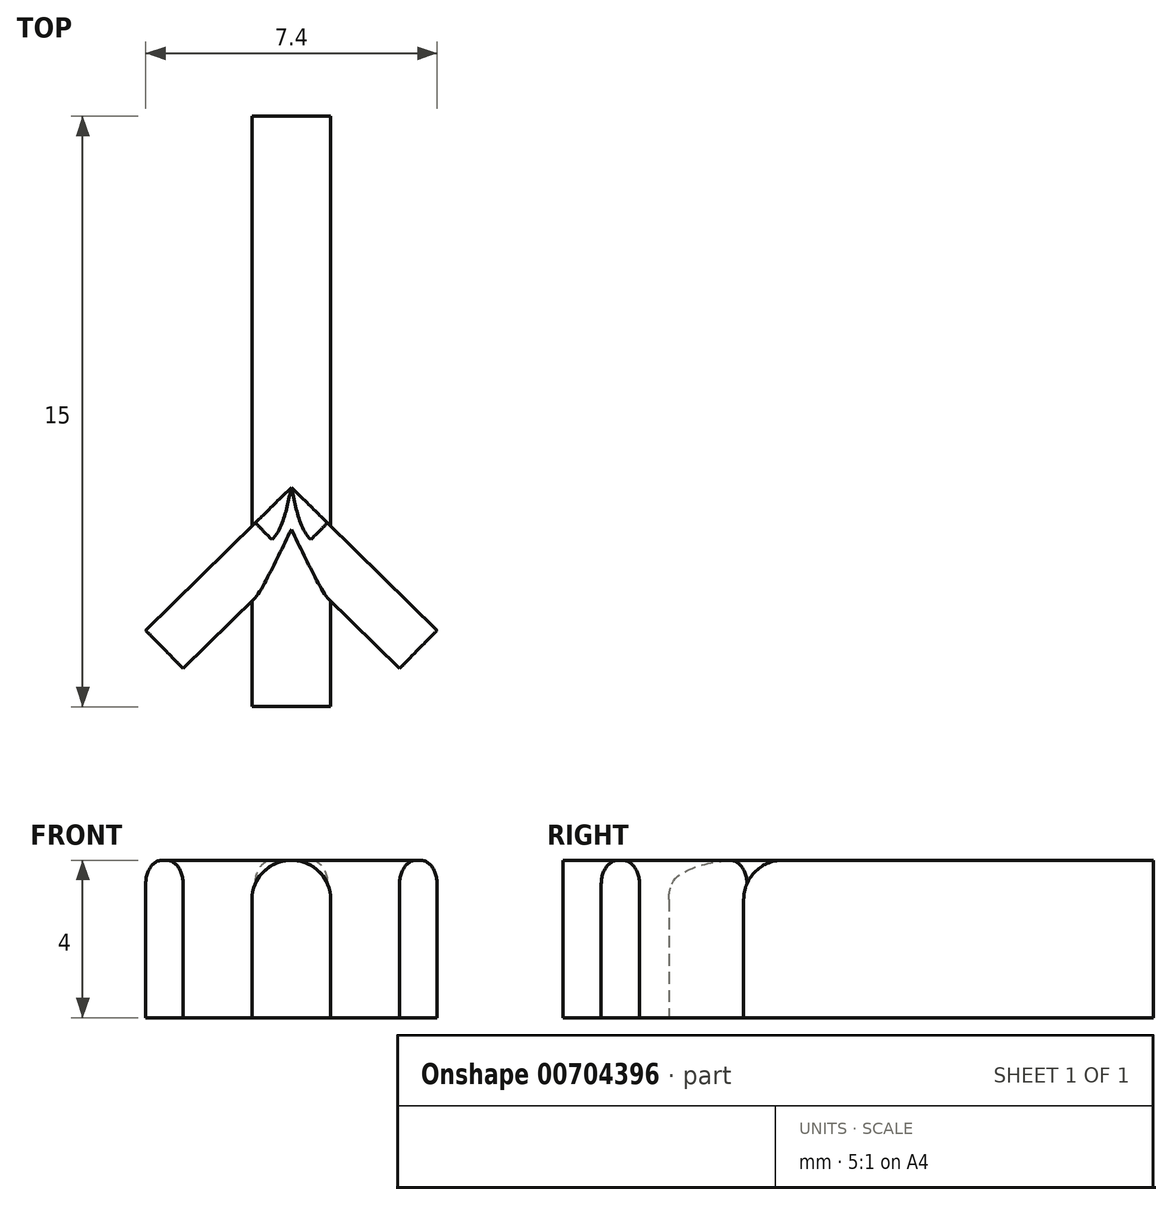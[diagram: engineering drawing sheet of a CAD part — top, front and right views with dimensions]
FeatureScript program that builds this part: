
annotation { "Feature Type Name" : "Feature", "Feature Type Description" : "" }
export const myFeature = defineFeature(function(context is Context, id is Id, definition is map)
    precondition{}
    {
        {
            var Q0;
            Q0=qCreatedBy(makeId("Top.planeOp"),FACE);
            var sketch = newSketch(context, id + "F0", { "sketchPlane" : qUnion([Q0])});
            skLineSegment(sketch, "E0", {"start": v(-1, 3.24) * mm, "end": v(-1, -7.17) * mm});
            skLineSegment(sketch, "E1", {"start": v(-1, 3.24) * mm, "end": v(0, 3.24) * mm});
            skLineSegment(sketch, "E2", {"start": v(-1, -7.17) * mm, "end": v(-3.7, -9.82) * mm});
            skLineSegment(sketch, "E3", {"start": v(-3.7, -9.82) * mm, "end": v(-2.75, -10.79) * mm});
            skLineSegment(sketch, "E4", {"start": v(-2.75, -10.79) * mm, "end": v(-1, -9.07) * mm});
            skLineSegment(sketch, "E5", {"start": v(-1, -9.07) * mm, "end": v(-1, -11.76) * mm});
            skLineSegment(sketch, "E6", {"start": v(-1, -11.76) * mm, "end": v(0, -11.76) * mm});
            skLineSegment(sketch, "E7.MirrorCS", {"start": v(1, 3.24) * mm, "end": v(0, 3.24) * mm});
            skLineSegment(sketch, "E8.MirrorCS", {"start": v(1, 3.24) * mm, "end": v(1, -7.17) * mm});
            skLineSegment(sketch, "E9.MirrorCS", {"start": v(1, -7.17) * mm, "end": v(3.7, -9.82) * mm});
            skLineSegment(sketch, "E10.MirrorCS", {"start": v(3.7, -9.82) * mm, "end": v(2.75, -10.79) * mm});
            skLineSegment(sketch, "E11.MirrorCS", {"start": v(2.75, -10.79) * mm, "end": v(1, -9.07) * mm});
            skLineSegment(sketch, "E12.MirrorCS", {"start": v(1, -9.07) * mm, "end": v(1, -11.76) * mm});
            skLineSegment(sketch, "E13.MirrorCS", {"start": v(1, -11.76) * mm, "end": v(0, -11.76) * mm});
            skSolve(sketch);
        }
        {
            var Q0;
            Q0=makeQuery(id+"F0.imprint","IMPRINT",FACE,{"disambiguationData":[TD([[makeQuery(id+"F0.imprint","IMPRINT",EDGE,{"derivedFrom":sQuery(id+"F0.wireOp",EDGE,"E0")}),1.0]])]});
            extrude(context, id + "F1", {"entities" : qUnion([Q0]), "depth" : 4 * mm, "offsetDistance" : 25 * mm});
        }
        {
            var Q0;
            Q0=makeQuery(id+"F1.opExtrude","CAP_EDGE",EDGE,{"disambiguationData":[OSD([sQuery(id+"F0.wireOp",EDGE,"E0")])],"isStart":false});
            var Q1;
            Q1=makeQuery(id+"F1.opExtrude","CAP_EDGE",EDGE,{"disambiguationData":[OSD([sQuery(id+"F0.wireOp",EDGE,"E8.MirrorCS")])],"isStart":false});
            fillet(context, id + "F2", {"entities" : qUnion([Q0, Q1]), "radius" : 1 * mm, "tangentPropagation" : true, "allowEdgeOverflow" : false});
        }
        {
            var Q0;
            Q0=makeQuery(id+"F1.opExtrude","CAP_EDGE",EDGE,{"disambiguationData":[OSD([sQuery(id+"F0.wireOp",EDGE,"E4")])],"isStart":false});
            var Q1;
            Q1=makeQuery(id+"F1.opExtrude","CAP_EDGE",EDGE,{"disambiguationData":[OSD([sQuery(id+"F0.wireOp",EDGE,"E2")])],"isStart":false});
            var Q2;
            Q2=makeQuery(id+"F1.opExtrude","CAP_EDGE",EDGE,{"disambiguationData":[OSD([sQuery(id+"F0.wireOp",EDGE,"E9.MirrorCS")])],"isStart":false});
            var Q3;
            Q3=makeQuery(id+"F1.opExtrude","CAP_EDGE",EDGE,{"disambiguationData":[OSD([sQuery(id+"F0.wireOp",EDGE,"E11.MirrorCS")])],"isStart":false});
            fillet(context, id + "F3", {"entities" : qUnion([Q0, Q1, Q2, Q3]), "radius" : 0.6 * mm, "tangentPropagation" : true, "allowEdgeOverflow" : false});
        }
        {
            var Q0;
            Q0=makeQuery(id+"F1.opExtrude","CAP_EDGE",EDGE,{"disambiguationData":[OSD([sQuery(id+"F0.wireOp",EDGE,"E5")])],"isStart":false});
            var Q1;
            Q1=makeQuery(id+"F1.opExtrude","CAP_EDGE",EDGE,{"disambiguationData":[OSD([sQuery(id+"F0.wireOp",EDGE,"E12.MirrorCS")])],"isStart":false});
            fillet(context, id + "F4", {"entities" : qUnion([Q0, Q1]), "radius" : 1 * mm, "tangentPropagation" : true, "allowEdgeOverflow" : false});
        }
    });
